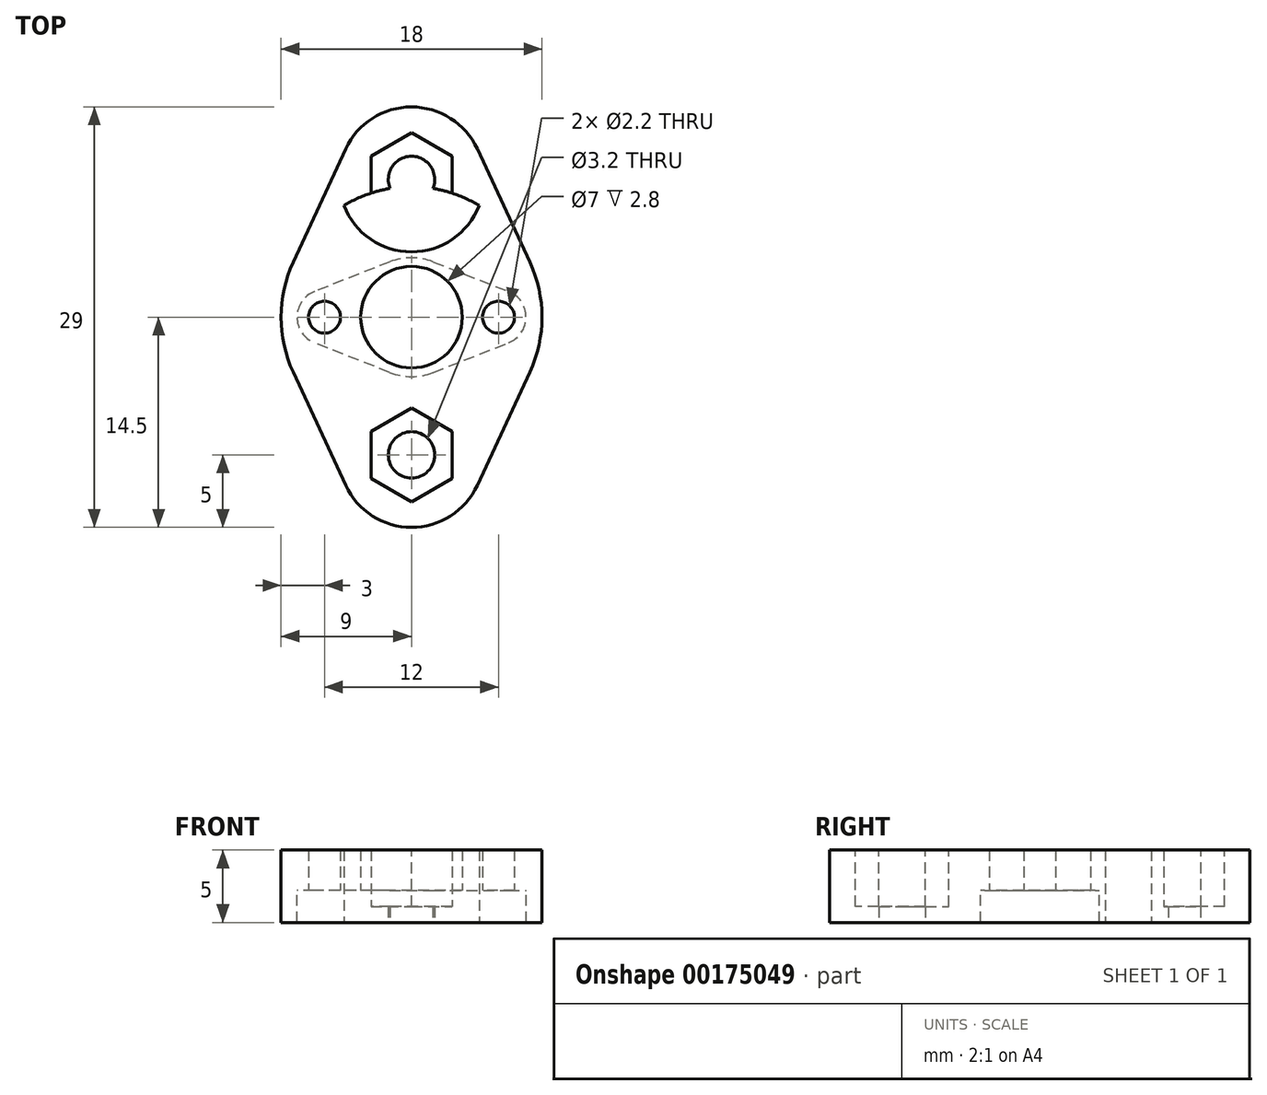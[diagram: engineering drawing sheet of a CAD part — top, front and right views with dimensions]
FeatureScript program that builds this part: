
annotation { "Feature Type Name" : "Feature", "Feature Type Description" : "" }
export const myFeature = defineFeature(function(context is Context, id is Id, definition is map)
    precondition{}
    {
        {
            var Q0;
            Q0=qCreatedBy(makeId("Top.planeOp"),FACE);
            var sketch = newSketch(context, id + "F0", { "sketchPlane" : qUnion([Q0])});
            skCircle(sketch, "E0", {"center": v(0, 0) * mm, "radius": 3.5 * mm});
            skLineSegment(sketch, "E1", {"start": v(0, 0) * mm, "end": v(6, 0) * mm, "construction": true});
            skCircle(sketch, "E2", {"center": v(6, 0) * mm, "radius": 1.1 * mm});
            skCircle(sketch, "E3.MirrorC", {"center": v(-6, 0) * mm, "radius": 1.1 * mm});
            skLineSegment(sketch, "E4", {"start": v(0, 0) * mm, "end": v(0, 9.5) * mm, "construction": true});
            skCircle(sketch, "E5", {"center": v(0, 9.5) * mm, "radius": 1.6 * mm});
            skCircle(sketch, "E6.MirrorC", {"center": v(0, -9.5) * mm, "radius": 1.6 * mm});
            skCircle(sketch, "E7", {"center": v(0, -9.5) * mm, "radius": 5 * mm});
            skCircle(sketch, "E8", {"center": v(0, 0) * mm, "radius": 9 * mm});
            skCircle(sketch, "E9", {"center": v(0, 9.5) * mm, "radius": 5 * mm});
            skLineSegment(sketch, "E10", {"start": v(8.16, -3.79) * mm, "end": v(4.54, -11.6) * mm});
            skLineSegment(sketch, "E11", {"start": v(-8.16, -3.79) * mm, "end": v(-4.54, -11.6) * mm});
            skLineSegment(sketch, "E12.MirrorCS", {"start": v(8.16, 3.79) * mm, "end": v(4.54, 11.6) * mm});
            skLineSegment(sketch, "E13.MirrorCS", {"start": v(-8.16, 3.79) * mm, "end": v(-4.54, 11.6) * mm});
            skSolve(sketch);
        }
        {
            var Q0;
            Q0 = qSketchRegion(id + "F0", true);
            var Q1;
            {var subQ0=sQuery(id+"F0.wireOp",EDGE,"E9");var subQ1=sQuery(id+"F0.wireOp",EDGE,"E8");var subQ2=makeQuery(id+"F0.imprint","INTERSECT",VERTEX,{"disambiguationData":[OD(0.0)],"derivedFrom":[subQ1,subQ0]});Q1=makeQuery(id+"F0.imprint","IMPRINT",FACE,{"disambiguationData":[TD([[makeQuery(id+"F0.imprint","IMPRINT",EDGE,{"disambiguationData":[TD([[subQ2,-1.0]])],"derivedFrom":subQ1}),1.0]])]});}
            var Q2;
            {var subQ0=sQuery(id+"F0.wireOp",EDGE,"E8");var subQ1=sQuery(id+"F0.wireOp",EDGE,"E7");var subQ2=makeQuery(id+"F0.imprint","INTERSECT",VERTEX,{"disambiguationData":[OD(0.0)],"derivedFrom":[subQ1,subQ0]});Q2=makeQuery(id+"F0.imprint","IMPRINT",FACE,{"disambiguationData":[TD([[makeQuery(id+"F0.imprint","IMPRINT",EDGE,{"disambiguationData":[TD([[subQ2,1.0]])],"derivedFrom":subQ1}),1.0]])]});}
            extrude(context, id + "F1", {"entities" : qUnion([Q0, Q1, Q2]), "depth" : 5 * mm});
        }
        {
            var Q0;
            Q0=makeQuery(id+"F1.opExtrude","CAP_FACE",FACE,{"disambiguationData":[OSD([sQuery(id+"F0.wireOp",EDGE,"E0"),sQuery(id+"F0.wireOp",EDGE,"E2"),sQuery(id+"F0.wireOp",EDGE,"E3.MirrorC"),sQuery(id+"F0.wireOp",EDGE,"E5"),sQuery(id+"F0.wireOp",EDGE,"E6.MirrorC"),sQuery(id+"F0.wireOp",EDGE,"E7"),sQuery(id+"F0.wireOp",EDGE,"E8"),sQuery(id+"F0.wireOp",EDGE,"E10"),sQuery(id+"F0.wireOp",EDGE,"E11"),sQuery(id+"F0.wireOp",EDGE,"E12.MirrorCS"),sQuery(id+"F0.wireOp",EDGE,"E13.MirrorCS"),sQuery(id+"F0.wireOp",EDGE,"E9")])],"isStart":false});
            var sketch = newSketch(context, id + "F2", { "sketchPlane" : qUnion([Q0])});
            skCircle(sketch, "E14.0", {"center": v(0, 9.5) * mm, "radius": 1.6 * mm});
            skCircle(sketch, "E15.cCircle", {"center": v(0, 9.5) * mm, "radius": 2.8 * mm, "construction": true});
            skLineSegment(sketch, "E15.0", {"start": v(2.8, 11.12) * mm, "end": v(2.8, 7.88) * mm});
            skLineSegment(sketch, "E15.1", {"start": v(2.8, 7.88) * mm, "end": v(0, 6.27) * mm});
            skLineSegment(sketch, "E15.2", {"start": v(0, 6.27) * mm, "end": v(-2.8, 7.88) * mm});
            skLineSegment(sketch, "E15.3", {"start": v(-2.8, 7.88) * mm, "end": v(-2.8, 11.12) * mm});
            skLineSegment(sketch, "E15.4", {"start": v(-2.8, 11.12) * mm, "end": v(0, 12.73) * mm});
            skLineSegment(sketch, "E15.5", {"start": v(0, 12.73) * mm, "end": v(2.8, 11.12) * mm});
            skPoint(sketch, "E15.0.midPoint", {"position": v(2.8, 9.5) * mm});
            skLineSegment(sketch, "E16.MirrorCS", {"start": v(0, -12.73) * mm, "end": v(2.8, -11.12) * mm});
            skLineSegment(sketch, "E17.MirrorCS", {"start": v(-2.8, -11.12) * mm, "end": v(0, -12.73) * mm});
            skLineSegment(sketch, "E18.MirrorCS", {"start": v(-2.8, -7.88) * mm, "end": v(-2.8, -11.12) * mm});
            skLineSegment(sketch, "E19.MirrorCS", {"start": v(0, -6.27) * mm, "end": v(-2.8, -7.88) * mm});
            skLineSegment(sketch, "E20.MirrorCS", {"start": v(2.8, -7.88) * mm, "end": v(0, -6.27) * mm});
            skLineSegment(sketch, "E21.MirrorCS", {"start": v(2.8, -11.12) * mm, "end": v(2.8, -7.88) * mm});
            skSolve(sketch);
        }
        {
            var Q0;
            Q0 = qSketchRegion(id + "F2", true);
            extrude(context, id + "F3", {"entities" : qUnion([Q0]), "operationType" : NewBodyOperationType.REMOVE, "oppositeDirection" : true, "depth" : 3.9 * mm});
        }
        {
            var Q0;
            Q0=makeQuery(id+"F1.opExtrude","CAP_FACE",FACE,{"disambiguationData":[OSD([sQuery(id+"F0.wireOp",EDGE,"E0"),sQuery(id+"F0.wireOp",EDGE,"E2"),sQuery(id+"F0.wireOp",EDGE,"E3.MirrorC"),sQuery(id+"F0.wireOp",EDGE,"E5"),sQuery(id+"F0.wireOp",EDGE,"E6.MirrorC"),sQuery(id+"F0.wireOp",EDGE,"E7"),sQuery(id+"F0.wireOp",EDGE,"E8"),sQuery(id+"F0.wireOp",EDGE,"E10"),sQuery(id+"F0.wireOp",EDGE,"E11"),sQuery(id+"F0.wireOp",EDGE,"E12.MirrorCS"),sQuery(id+"F0.wireOp",EDGE,"E13.MirrorCS"),sQuery(id+"F0.wireOp",EDGE,"E9")])],"isStart":false});
            var sketch = newSketch(context, id + "F4", { "sketchPlane" : qUnion([Q0])});
            skArc(sketch, "E22", {"start": v(-6.7, 1.77) * mm, "mid": v(-7.9, 0) * mm, "end": v(-6.7, -1.77) * mm});
            skArc(sketch, "E23.MirrorC", {"start": v(6.7, 1.77) * mm, "mid": v(7.9, 0) * mm, "end": v(6.7, -1.77) * mm});
            skArc(sketch, "E24", {"start": v(-1.5, -3.81) * mm, "mid": v(0, -4.1) * mm, "end": v(1.5, -3.81) * mm});
            skLineSegment(sketch, "E25", {"start": v(-1.5, 3.81) * mm, "end": v(-6.7, 1.77) * mm});
            skLineSegment(sketch, "E26.MirrorCS", {"start": v(1.5, 3.81) * mm, "end": v(6.7, 1.77) * mm});
            skLineSegment(sketch, "E27.MirrorCS", {"start": v(1.5, -3.81) * mm, "end": v(6.7, -1.77) * mm});
            skLineSegment(sketch, "E28.MirrorCS", {"start": v(-1.5, -3.81) * mm, "end": v(-6.7, -1.77) * mm});
            skArc(sketch, "E29.trimOffspring", {"start": v(1.5, 3.81) * mm, "mid": v(0, 4.1) * mm, "end": v(-1.5, 3.81) * mm});
            skSolve(sketch);
        }
        {
            var Q0;
            Q0 = qSketchRegion(id + "F4", true);
            extrude(context, id + "F5", {"entities" : qUnion([Q0]), "operationType" : NewBodyOperationType.REMOVE, "oppositeDirection" : true, "depth" : 25 * mm, "hasSecondDirection" : true, "secondDirectionOppositeDirection" : true, "secondDirectionDepth" : 2.8 * mm});
        }
    });
